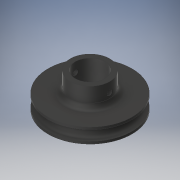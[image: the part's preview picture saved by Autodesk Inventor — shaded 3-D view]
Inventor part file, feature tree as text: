
AUTODESK INVENTOR PART (.ipt)
format: ipt  version: 2019 (Build 230136000, 136)  size: 184,832 bytes
history: native  units: in
note: dims shown in document units (in); Inventor stores cm internally (conversion verified against a paired STEP export)
features: sketch x4, extrude x3, revolve x1, mirror x1, fillet x1, projected_geometry x1
ambient origin geometry x8: Origin, YZ Plane, XZ Plane, XY Plane, X Axis, Y Axis, Z Axis, Center Point
bodies: Solid1 (feature_tree)
feature tree (11):
  revolve  "Revolution1"  [1 undecoded]
  mirror  "Mirror1"
  extrude  "Extrusion1"  TaperAngle=90.0deg  [1 undecoded]
  extrude  "Extrusion2"  Depth=1.0in TaperAngle=0.0deg
  extrude  "Extrusion3"  Depth=0.25in TaperAngle=0.0deg
  fillet  "Fillet1"  Radius=0.0625in
  sketch  "Sketch1"  dims[d2=0.0635in d4=0.0938in]
  sketch  "Sketch2"  dims[d5=0.0318in d6=90.0deg]
  sketch  "Sketch3"  dims[d7=0.375in d8=1.0in d9=0.0in]
  sketch  "Sketch4"  dims[d10=0.0625in d11=0.25in d12=0.0in d13=0.0625in d14=0.275in d15=0.0in d16=0.5in d17=0.0625in]
  projected_geometry  "Projected Loop1"
note: 2 required parameter values undecoded (feature->parameter linkage not recoverable at this tier; creation-order binding heuristic only, values carry confidence <= 0.55)